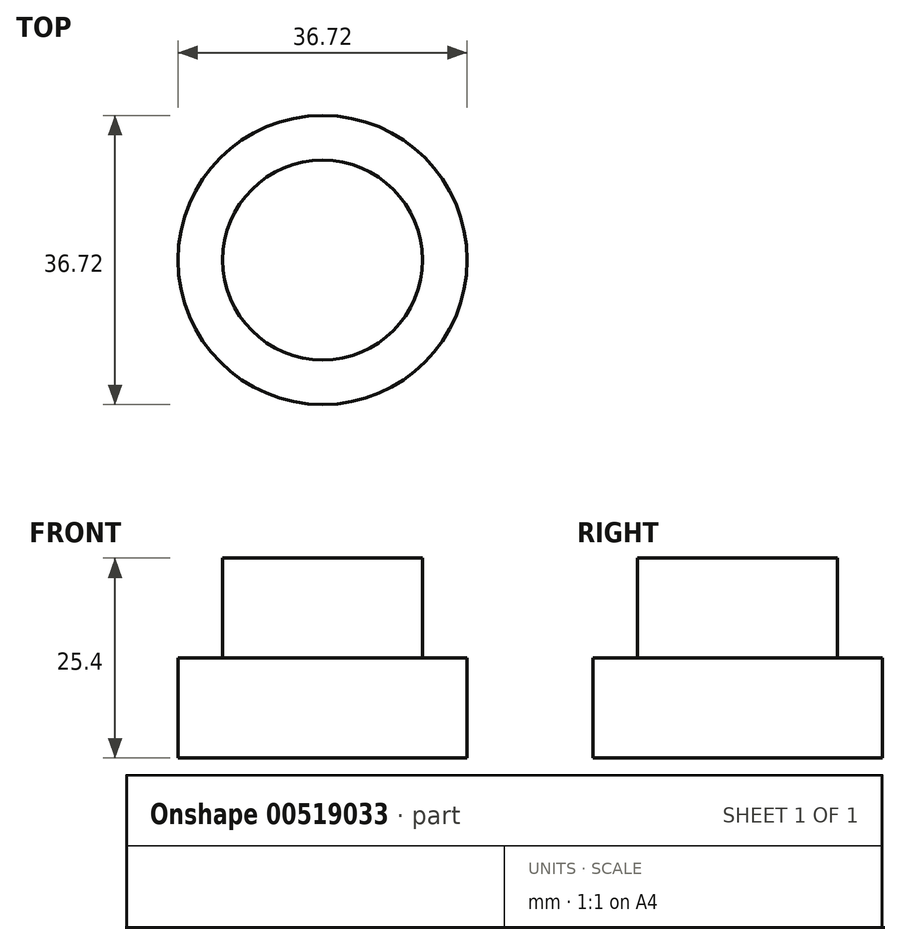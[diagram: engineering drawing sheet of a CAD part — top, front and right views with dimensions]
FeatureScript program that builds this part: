
annotation { "Feature Type Name" : "Feature", "Feature Type Description" : "" }
export const myFeature = defineFeature(function(context is Context, id is Id, definition is map)
    precondition{}
    {
        {
            var Q0;
            Q0=qCreatedBy(makeId("Front.planeOp"),FACE);
            var sketch = newSketch(context, id + "F0", { "sketchPlane" : qUnion([Q0])});
            skLineSegment(sketch, "E0", {"start": v(0, 11.12) * mm, "end": v(0, 0) * mm});
            skSolve(sketch);
        }
        {
            var Q0;
            Q0=qCreatedBy(makeId("Front.planeOp"),FACE);
            var sketch = newSketch(context, id + "F1", { "sketchPlane" : qUnion([Q0])});
            skLineSegment(sketch, "E1", {"start": v(12.7, 25.4) * mm, "end": v(12.7, 12.7) * mm});
            skLineSegment(sketch, "E2", {"start": v(18.36, 0) * mm, "end": v(18.36, 12.7) * mm});
            skLineSegment(sketch, "E3", {"start": v(12.7, 12.7) * mm, "end": v(18.36, 12.7) * mm});
            skLineSegment(sketch, "E4", {"start": v(12.7, 25.4) * mm, "end": v(12.7, 25.4) * mm});
            skLineSegment(sketch, "E5", {"start": v(12.7, 25.4) * mm, "end": v(0, 25.4) * mm});
            skLineSegment(sketch, "E6", {"start": v(0, 25.4) * mm, "end": v(0, 0) * mm});
            skPoint(sketch, "E7.MirrorCS.end.orphan", {"position": v(18.36, 0) * mm});
            skPoint(sketch, "E8.MirrorCS.start.orphan", {"position": v(12.7, 0) * mm});
            skLineSegment(sketch, "E9", {"start": v(0, 0) * mm, "end": v(18.36, 0) * mm});
            skLineSegment(sketch, "E10", {"start": v(18.36, 12.7) * mm, "end": v(18.36, 0) * mm});
            skSolve(sketch);
        }
        {
            var Q0;
            Q0=makeQuery(id+"F1.imprint","IMPRINT",FACE,{"disambiguationData":[TD([[makeQuery(id+"F1.imprint","IMPRINT",EDGE,{"derivedFrom":sQuery(id+"F1.wireOp",EDGE,"E3")}),-1.0]])]});
            var Q1;
            Q1=sQuery(id+"F0.wireOp",EDGE,"E0");
            revolve(context, id + "F2", {"entities" : qUnion([Q0]), "axis" : qUnion([Q1]), "revolveType" : RevolveType.FULL});
        }
    });
